# Revit family: Ceileo-RD
name_source: partatom
category: Lighting Fixtures
revit_build: Autodesk Revit Architecture 2012 (Build: 20110309_2315(x64)
units: mm (PartAtom-declared; Revit-internal decimal feet)

## types (12) — shared parameters
Apparent Load = 55 VA
Default Elevation = 48"
Description = Ceileo is a commercial grade LED canopy luminaire that utilizes high powered LED’s with precise efficient optical control and on board wattage and lumen choices.
Glass = Hubbell- White Glass
Lamp = LED Lamp
Manufacturer = Beacon Lighting
Manufacturer Fax = (941) 751-5535
Model = CLO RD
Nominal Watts = 55 W
Product Documentation Link = http://www.beaconproducts.com
Product Page URL = http://www.beaconproducts.com
URL = http://www.beaconproducts.com
Voltage = 120 V

## per-type parameters (varying)
| type | Backbox | Photometric Web | Wattage Comments |
| CLO RD-BBT | Hubbell- Paint- Black Textured | Web CLO : CLO-24NB-55-4K-3X5 |  |
| CLO RD-BMT | Hubbell- Paint- Black Matte Textured | Web CLO : CLO-24NB-55-3K-5X5 | 55 W |
| CLO RD-WHT | Hubbell- Paint- White | Web CLO : CLO-24NB-55-3K-5X5 |  |
| CLO RD-BZT | Hubbell- Paint- Bronze Textured | Web CLO : CLO-24NB-55-3K-5X5 |  |
| CLO RD-MBT | Hubbell- Paint- Mettalic Bronze Textured | Web CLO : CLO-24NB-55-3K-5X5 |  |
| CLO RD-DBT | Hubbell- Paint- Dark  Bronze Textured | Web CLO : CLO-24NB-55-3K-5X5 |  |
| CLO RD-GYS | Hubbell- Paint- Grey smooth | Web CLO : CLO-24NB-55-3K-5X5 |  |
| CLO RD-DPS | Hubbell- Paint- Dark Platinum Smooth | Web CLO : CLO-24NB-55-3K-5X5 |  |
| CLO RD-GNT | Hubbell- Paint- Green Textured | Web CLO : CLO-24NB-55-3K-5X5 |  |
| CLO RD-MST | Hubbell- Paint- Mettallic Silver Textured | Web CLO : CLO-24NB-55-3K-5X5 |  |
| CLO RD-MTT | Hubbell- Paint- Metallic titanium textured | Web CLO : CLO-24NB-55-3K-5X5 |  |
| CLO RD-OWI | Hubbell- Paint- Old World Iron | Web CLO : CLO-24NB-55-3K-5X5 |  |

## geometry (parser evidence)
native form markers: Blend x15, Sweep x2
no freeform markers — native parametric forms only
